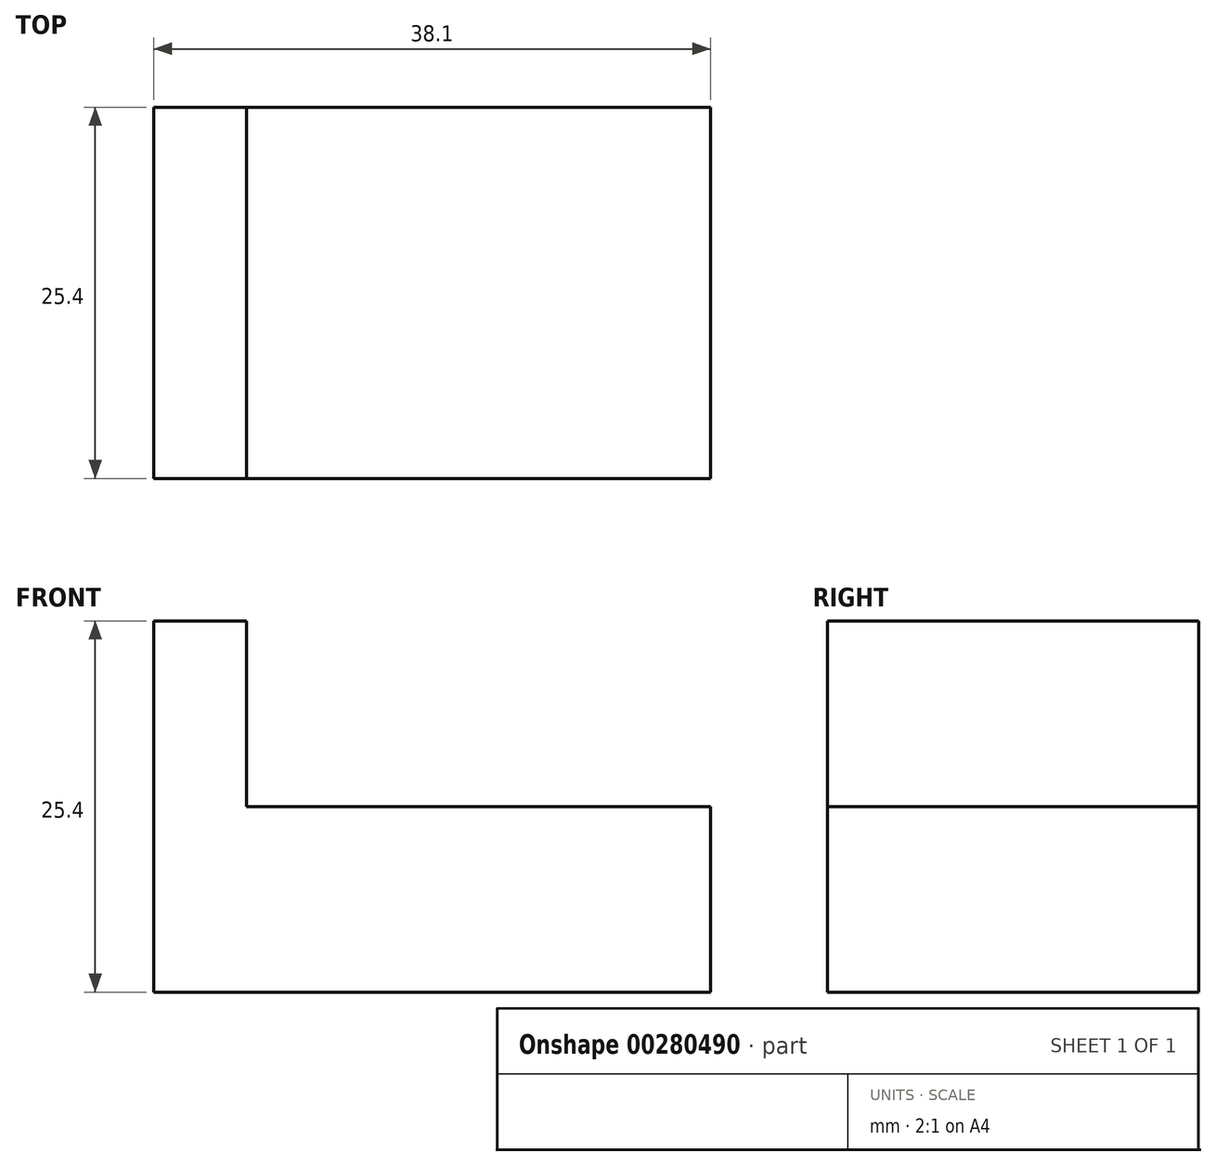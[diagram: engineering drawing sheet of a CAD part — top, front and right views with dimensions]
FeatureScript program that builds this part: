
annotation { "Feature Type Name" : "Feature", "Feature Type Description" : "" }
export const myFeature = defineFeature(function(context is Context, id is Id, definition is map)
    precondition{}
    {
        {
            var Q0;
            Q0=qCreatedBy(makeId("Top.planeOp"),FACE);
            var sketch = newSketch(context, id + "F0", { "sketchPlane" : qUnion([Q0])});
            skLineSegment(sketch, "E0.bottom", {"start": v(19.05, 12.7) * mm, "end": v(-19.05, 12.7) * mm});
            skLineSegment(sketch, "E0.top", {"start": v(19.05, -12.7) * mm, "end": v(-19.05, -12.7) * mm});
            skLineSegment(sketch, "E0.left", {"start": v(19.05, 12.7) * mm, "end": v(19.05, -12.7) * mm});
            skLineSegment(sketch, "E0.right", {"start": v(-19.05, 12.7) * mm, "end": v(-19.05, -12.7) * mm});
            skPoint(sketch, "E0.middle", {"position": v(0, 0) * mm});
            skLineSegment(sketch, "E1", {"start": v(-12.7, 12.7) * mm, "end": v(-12.7, -12.7) * mm});
            skSolve(sketch);
        }
        {
            var Q0;
            {var subQ0=sQuery(id+"F0.wireOp",EDGE,"E0.left");Q0=makeQuery(id+"F0.imprint","IMPRINT",FACE,{"disambiguationData":[TD([[makeQuery(id+"F0.imprint","IMPRINT",EDGE,{"derivedFrom":subQ0}),-1.0]])]});}
            extrude(context, id + "F1", {"entities" : qUnion([Q0]), "depth" : 12.7 * mm});
        }
        {
            var Q0;
            {var subQ0=sQuery(id+"F0.wireOp",EDGE,"E0.right");Q0=makeQuery(id+"F0.imprint","IMPRINT",FACE,{"disambiguationData":[TD([[makeQuery(id+"F0.imprint","IMPRINT",EDGE,{"derivedFrom":subQ0}),1.0]])]});}
            extrude(context, id + "F2", {"entities" : qUnion([Q0]), "operationType" : NewBodyOperationType.ADD, "depth" : 25.4 * mm});
        }
    });
